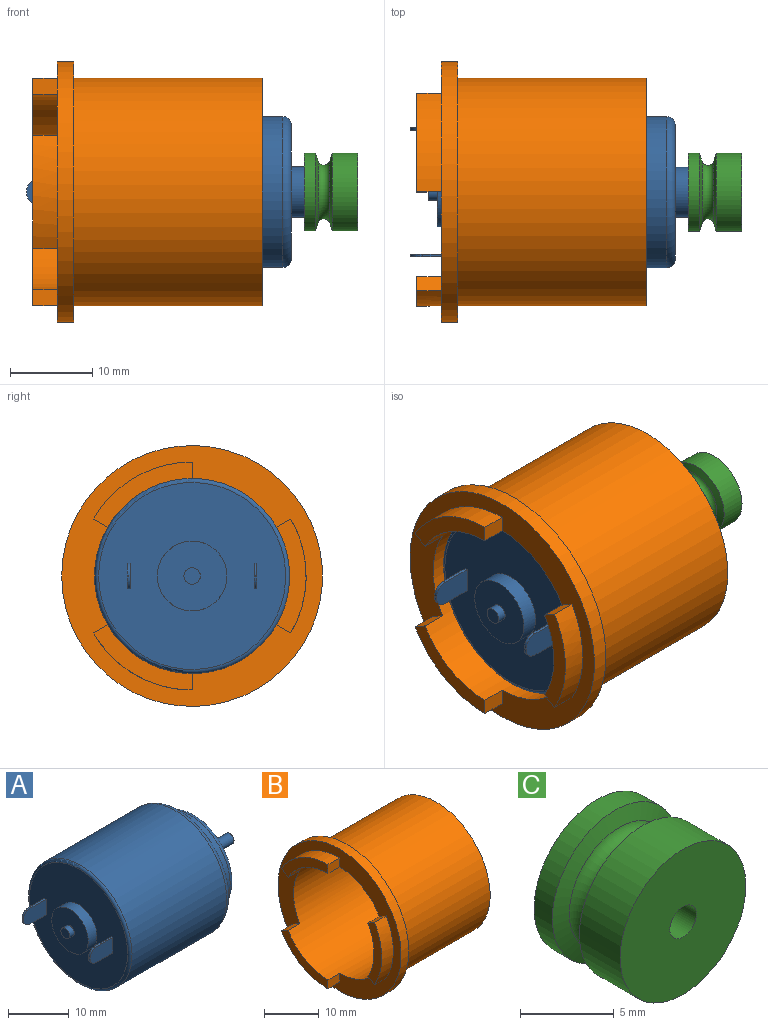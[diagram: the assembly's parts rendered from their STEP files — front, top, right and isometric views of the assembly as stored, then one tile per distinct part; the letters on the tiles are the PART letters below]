
ASSEMBLY  parts=3 mates=2
PART A: 30 faces, bbox 40.4x25.8x25.8 mm
  f0: plane 22.8x22.8mm, normal (-1,0,0), area 349.3mm2, adj f10,f15,f16,f17,f18,f19,f21,f22
  f1: plane 8.5x8.5mm, normal (-1,0,0), area 53.6mm2, adj f10,f11
  f2: cylinder r=11.9mm len=23.8mm, axis (-1,0,0), area 1644.9mm2, adj f14,f15
  f3: plane 21.8x21.8mm, normal (1,0,0), area 107.3mm2, adj f4,f14
  f4: cylinder r=9.2mm len=18.4mm, axis (-1,0,0), area 144.5mm2, adj f3,f13
  f5: plane 16.4x16.4mm, normal (1,0,0), area 182mm2, adj f6,f13
  f6: cylinder r=3.05mm len=6.1mm, axis (-1,0,0), area 30.7mm2, adj f5,f7
  f7: plane 6.1x6.1mm, normal (1,0,0), area 26.1mm2, adj f6,f8
  f8: cylinder r=1mm len=6.5mm, axis (-1,0,0), area 40.8mm2, adj f7,f9
  f9: plane 2x2mm, normal (1,0,0), area 3.1mm2, adj f8
  f10: cylinder r=4.25mm len=8.5mm, axis (1,0,0), area 53.4mm2, adj f0,f1
  f11: cylinder r=1mm len=2mm, axis (1,0,0), area 7mm2, adj f1,f12
  f12: plane 2x2mm, normal (-1,0,0), area 3.1mm2, adj f11
  f13: torus R=8.2mm, axis (-1,0,0), area 87.2mm2, adj f4,f5
  f14: torus R=10.9mm, axis (-1,0,0), area 113.9mm2, adj f2,f3
  f15: torus R=11.4mm, axis (1,0,0), area 57.8mm2, adj f0,f2
  f16: plane 5.26x3.15mm, normal (0,1,0), area 15.6mm2, adj f0,f17,f19,f20,f28,f29
  f17: plane 3.76x0.35mm, normal (0,0,-1), area 1.3mm2, adj f0,f16,f18,f28
  f18: plane 5.26x3.15mm, normal (0,-1,0), area 15.6mm2, adj f0,f17,f19,f20,f28,f29
  f19: plane 3.76x0.35mm, normal (0,0,1), area 1.3mm2, adj f0,f16,f18,f29
  f20: plane 0.35x0.15mm, normal (-1,0,0), area 0.1mm2, adj f16,f18,f28,f29
  f21: plane 5.26x3.15mm, normal (0,1,0), area 15.6mm2, adj f0,f22,f24,f25,f26,f27
  f22: plane 3.76x0.35mm, normal (0,0,-1), area 1.3mm2, adj f0,f21,f23,f26
  f23: plane 5.26x3.15mm, normal (0,-1,0), area 15.6mm2, adj f0,f22,f24,f25,f26,f27
  f24: plane 3.76x0.35mm, normal (0,0,1), area 1.3mm2, adj f0,f21,f23,f27
  f25: plane 0.35x0.15mm, normal (-1,0,0), area 0.1mm2, adj f21,f23,f26,f27
  f26: cylinder r=1.5mm len=1.5mm, axis (0,1,0), area 0.8mm2, adj f21,f22,f23,f25
  f27: cylinder r=1.5mm len=1.5mm, axis (0,-1,0), area 0.8mm2, adj f21,f23,f24,f25
  f28: cylinder r=1.5mm len=1.5mm, axis (0,1,0), area 0.8mm2, adj f16,f17,f18,f20
  f29: cylinder r=1.5mm len=1.5mm, axis (0,-1,0), area 0.8mm2, adj f16,f18,f19,f20
PART B: 18 faces, bbox 28x31.8x31.8 mm
  f0: cylinder r=13.9mm len=12.04mm, axis (1,0,0), area 43.7mm2, adj f3,f4,f10,f17
  f1: cylinder r=11.9mm len=28mm, axis (1,0,0), area 1981.4mm2, adj f2,f3,f4,f5,f6,f7,f10,f14
  f2: plane 3x1.73mm, normal (0,0.5,0.87), area 6mm2, adj f1,f9,f10,f15
  f3: plane 3x1.73mm, normal (0,0.5,-0.87), area 6mm2, adj f0,f1,f10,f17
  f4: plane 3x2mm, normal (0,-1,0), area 6mm2, adj f0,f1,f10,f17
  f5: plane 3x1.73mm, normal (0,0.5,0.87), area 6mm2, adj f1,f8,f10,f16
  f6: plane 3x1.73mm, normal (0,0.5,-0.87), area 6mm2, adj f1,f8,f10,f16
  f7: plane 3x2mm, normal (0,-1,0), area 6mm2, adj f1,f9,f10,f15
  f8: cylinder r=13.9mm len=13.9mm, axis (1,0,0), area 43.7mm2, adj f5,f6,f10,f16
  f9: cylinder r=13.9mm len=12.04mm, axis (1,0,0), area 43.7mm2, adj f2,f7,f10,f15
  f10: plane 31.8x31.8mm, normal (-1,0,0), area 268.3mm2, adj f0,f1,f2,f3,f4,f5,f6,f7
  f11: cylinder r=15.9mm len=31.8mm, axis (1,0,0), area 199.8mm2, adj f10,f12
  f12: plane 31.8x31.8mm, normal (1,0,0), area 187.2mm2, adj f11,f13
  f13: cylinder r=13.9mm len=27.8mm, axis (1,0,0), area 2008.7mm2, adj f12,f14
  f14: plane 27.8x27.8mm, normal (1,0,0), area 162.1mm2, adj f1,f13
  f15: plane 12.05x7.95mm, normal (-1,0,0), area 27mm2, adj f1,f2,f7,f9
  f16: plane 13.91x3.6mm, normal (-1,0,0), area 27mm2, adj f1,f5,f6,f8
  f17: plane 12.04x7.95mm, normal (-1,0,0), area 27mm2, adj f0,f1,f3,f4
PART C: 8 faces, bbox 9.5x6.5x9.5 mm
  f0: torus R=4mm, axis (0,-1,0), area 41mm2, adj f1,f6
  f1: cone r=3.77mm half-angle=72.5deg, axis (0,1,0), area 27.4mm2, adj f0,f2
  f2: cylinder r=4.75mm len=9.5mm, axis (0,-1,0), area 41.1mm2, adj f1,f3
  f3: plane 9.5x9.5mm, normal (0,1,0), area 67.7mm2, adj f2,f7
  f4: plane 9.5x9.5mm, normal (0,-1,0), area 67.7mm2, adj f5,f7
  f5: cylinder r=4.75mm len=9.5mm, axis (0,-1,0), area 91.8mm2, adj f4,f6
  f6: cone r=3.77mm half-angle=72.5deg, axis (0,-1,0), area 27.4mm2, adj f0,f5
  f7: cylinder r=1mm len=6.5mm, axis (0,1,0), area 40.8mm2, adj f3,f4
PLACE A at identity
PLACE B at identity fixed
PLACE C rot(axis=(-0.58,0.58,0.58),120deg) t=(31,0,0)mm
MATE fastened C.f7 <-> A.f2  axis (1,0,0) through (35.1,0,0)mm
MATE fastened A.f2 <-> B.f0  axis (1,0,0) through (23.5,0,0)mm
